# Revit family: 6885 - 3m Installation
name_source: partatom
category: Generic Models
units: mm (PartAtom-declared; Revit-internal decimal feet)

## family parameters
Base Level = No
Can host rebar = Yes
Construction Type = No
Fascia Depth = No
Subcategory = Normal
Thickness = No

## types (1)
- Standard
    COBieAccessibilityPerformance = .
    COBieAssetIdentifier = .
    COBieAssetType = Fixed
    COBieBarCode = .
    COBieCodePerformance = .
    COBieColour = Any RAL
    COBieConstituents = .
    COBieCost = .
    COBieCreatedBy = Frontier Pitts Ltd.
    COBieCreatedOn = 15/07/2025 00:00:00
    COBieDescription = 3m ATTB80 Blocker
    COBieDocumentationCertificates = www.frontierpitts.com
    COBieDocumentationTechnical = www.frontierpitts.com
    COBieDocumnetationInstallationGuide = www.frontierpitts.com
    COBieDocumnetationLiterature = www.frontierpitts.com
    COBieDurationUnit = Years
    COBieExpectedLife = 15
    COBieFeatures = .
    COBieFinish = .
    COBieGrade = .
    COBieInstallationDate = .
    COBieManufacturer = Frontier Pitts Ltd.
    COBieMaterial = Steel
    COBieModelNumber = 6885-03
    COBieName = 3m ATTB80 Blocker
    COBieProductionYear = 2025
    COBieReferenceStandard = .
    COBieReplacementCost = .
    COBieSerialNumber = 6885-03
    COBieShape = Rectangle
    COBieSize = .
    COBieSpareParts = .
    COBieTypeName = Description
    COBieWarrantyDescription = 1 Year Parts & Labour
    COBieWarrantyDurationLabour = 1
    COBieWarrantyDurrationParts = 1
    COBieWarrantyDurrationUnit = Years
    COBieWarrantyGuarantorLabour = www.frontierpitts.com
    COBieWarrantyGuarantorParts = www.frontierpitts.com
    COBieWarrantyStartDate = .
    Is parametric = 0 mm  [stored 0 ft]
    Model = Description

note: [stored X ft] marks values corroborated as IEEE doubles in the binary element streams (Revit-internal decimal feet)

## geometry (parser evidence)
native form markers: Sweep x3
no freeform markers — native parametric forms only
